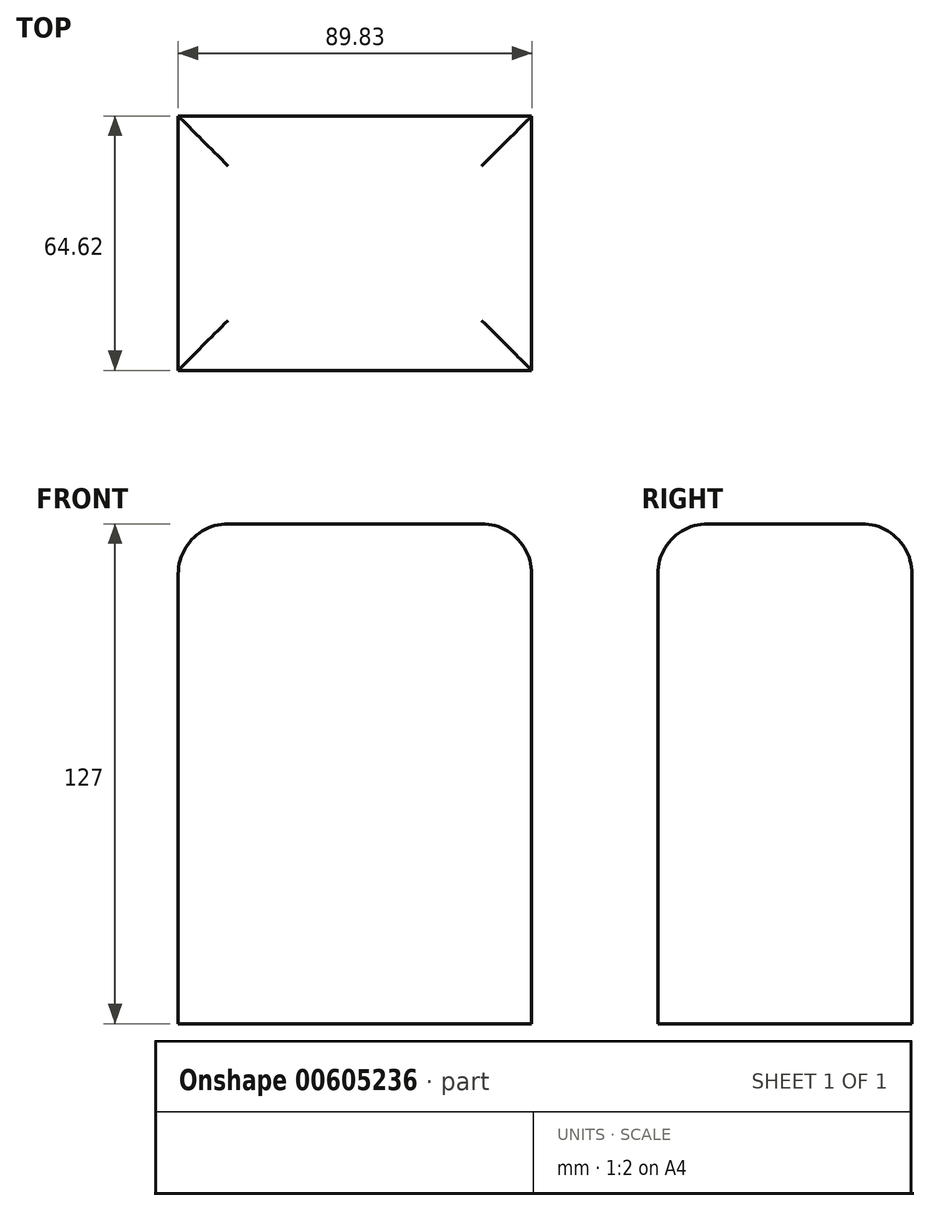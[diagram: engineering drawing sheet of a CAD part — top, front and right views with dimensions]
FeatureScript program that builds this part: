
annotation { "Feature Type Name" : "Feature", "Feature Type Description" : "" }
export const myFeature = defineFeature(function(context is Context, id is Id, definition is map)
    precondition{}
    {
        {
            var Q0;
            Q0=qCreatedBy(makeId("Top.planeOp"),FACE);
            var sketch = newSketch(context, id + "F0", { "sketchPlane" : qUnion([Q0])});
            skLineSegment(sketch, "E0.bottom", {"start": v(-47.67, 41.02) * mm, "end": v(42.16, 41.02) * mm});
            skLineSegment(sketch, "E0.top", {"start": v(-47.67, -23.6) * mm, "end": v(42.16, -23.6) * mm});
            skLineSegment(sketch, "E0.left", {"start": v(-47.67, 41.02) * mm, "end": v(-47.67, -23.6) * mm});
            skLineSegment(sketch, "E0.right", {"start": v(42.16, 41.02) * mm, "end": v(42.16, -23.6) * mm});
            skSolve(sketch);
        }
        {
            var Q0;
            Q0 = qSketchRegion(id + "F0", true);
            extrude(context, id + "F1", {"entities" : qUnion([Q0]), "depth" : 127 * mm, "offsetDistance" : 25.4 * mm});
        }
        {
            var Q0;
            Q0=makeQuery(id+"F1.opExtrude","CAP_EDGE",EDGE,{"disambiguationData":[OSD([sQuery(id+"F0.wireOp",EDGE,"E0.right")])],"isStart":false});
            var Q1;
            Q1=makeQuery(id+"F1.opExtrude","CAP_EDGE",EDGE,{"disambiguationData":[OSD([sQuery(id+"F0.wireOp",EDGE,"E0.top")])],"isStart":false});
            var Q2;
            Q2=makeQuery(id+"F1.opExtrude","CAP_EDGE",EDGE,{"disambiguationData":[OSD([sQuery(id+"F0.wireOp",EDGE,"E0.bottom")])],"isStart":false});
            var Q3;
            Q3=makeQuery(id+"F1.opExtrude","CAP_FACE",FACE,{"disambiguationData":[OSD([sQuery(id+"F0.wireOp",EDGE,"E0.bottom"),sQuery(id+"F0.wireOp",EDGE,"E0.top"),sQuery(id+"F0.wireOp",EDGE,"E0.left"),sQuery(id+"F0.wireOp",EDGE,"E0.right")])],"isStart":false});
            fillet(context, id + "F2", {"entities" : qUnion([Q0, Q1, Q2, Q3]), "radius" : 12.7 * mm, "tangentPropagation" : true, "allowEdgeOverflow" : false});
        }
    });
